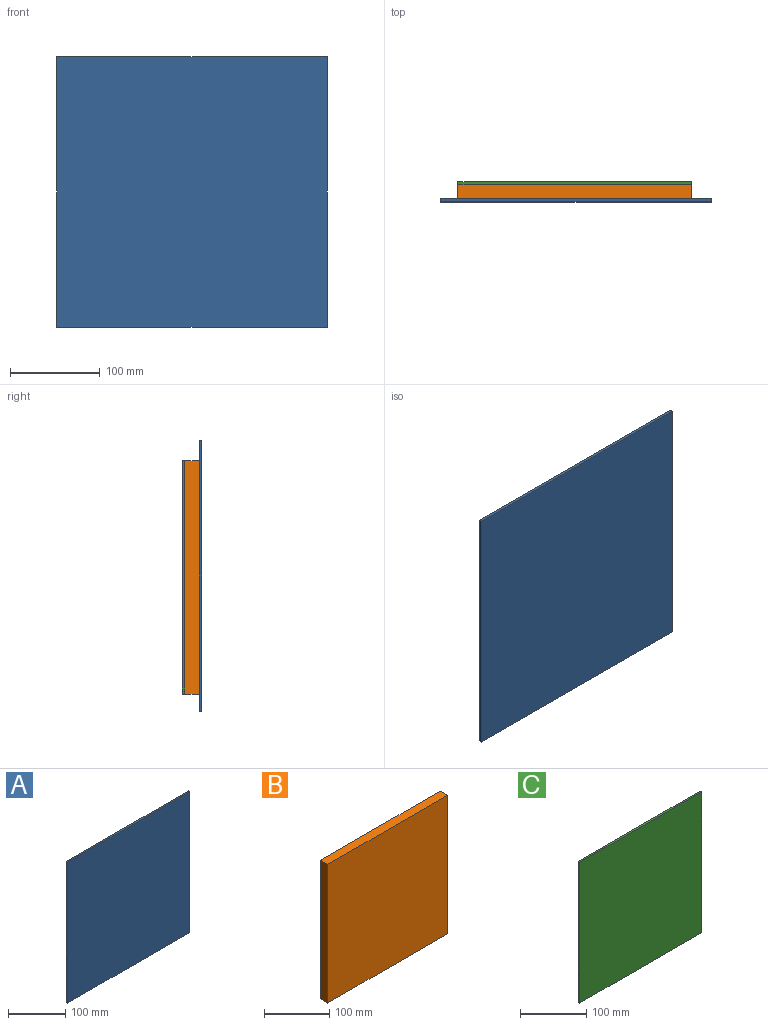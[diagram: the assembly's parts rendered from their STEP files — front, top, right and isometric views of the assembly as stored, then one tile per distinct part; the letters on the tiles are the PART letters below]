
ASSEMBLY  parts=3 mates=2
PART A: 6 faces, bbox 301.6x3.2x301.6 mm
  f0: plane 301.63x3.18mm, normal (0,0,-1), area 957.7mm2, adj f1,f3,f4,f5
  f1: plane 301.63x3.18mm, normal (1,0,0), area 957.7mm2, adj f0,f2,f4,f5
  f2: plane 301.63x3.18mm, normal (0,0,1), area 957.7mm2, adj f1,f3,f4,f5
  f3: plane 301.63x3.18mm, normal (-1,0,0), area 957.7mm2, adj f0,f2,f4,f5
  f4: plane 301.63x301.63mm, normal (0,-1,0), area 90977.6mm2, adj f0,f1,f2,f3
  f5: plane 301.63x301.63mm, normal (0,1,0), area 90977.6mm2, adj f0,f1,f2,f3
PART B: 6 faces, bbox 260.4x15.9x260.4 mm
  f0: plane 260.35x15.88mm, normal (0,0,-1), area 4133.1mm2, adj f1,f3,f4,f5
  f1: plane 260.35x15.88mm, normal (1,0,0), area 4133.1mm2, adj f0,f2,f4,f5
  f2: plane 260.35x15.88mm, normal (0,0,1), area 4133.1mm2, adj f1,f3,f4,f5
  f3: plane 260.35x15.88mm, normal (-1,0,0), area 4133.1mm2, adj f0,f2,f4,f5
  f4: plane 260.35x260.35mm, normal (0,-1,0), area 67782.1mm2, adj f0,f1,f2,f3
  f5: plane 260.35x260.35mm, normal (0,1,0), area 67782.1mm2, adj f0,f1,f2,f3
PART C: 6 faces, bbox 260.4x3.2x260.4 mm
  f0: plane 260.35x3.18mm, normal (0,0,-1), area 826.6mm2, adj f1,f3,f4,f5
  f1: plane 260.35x3.18mm, normal (1,0,0), area 826.6mm2, adj f0,f2,f4,f5
  f2: plane 260.35x3.18mm, normal (0,0,1), area 826.6mm2, adj f1,f3,f4,f5
  f3: plane 260.35x3.18mm, normal (-1,0,0), area 826.6mm2, adj f0,f2,f4,f5
  f4: plane 260.35x260.35mm, normal (0,-1,0), area 67782.1mm2, adj f0,f1,f2,f3
  f5: plane 260.35x260.35mm, normal (0,1,0), area 67782.1mm2, adj f0,f1,f2,f3
PLACE A t=(-306.64,55.71,-26.99)mm
PLACE B t=(-308.23,71.59,-28.57)mm
PLACE C t=(-308.23,74.76,-28.57)mm
MATE fastened B.f5 <-> C.f4  axis (0,1,0) through (159.74,71.59,-28.57)mm
MATE fastened A.f5 <-> B.f4  axis (0,1,0) through (161.32,55.71,-26.99)mm
